# Revit family: BAS-IP_Абонетское устройство_SP-03
name_source: partatom
category: Устройства связи
units: mm (PartAtom-declared; Revit-internal decimal feet)

## family parameters
Всегда вертикально = Да
На основе рабочей плоскости = Нет
Общий = Нет
При загрузке вырезать с полостями = Нет
Размер круглого соединителя = Использовать диаметр
Сохранять ориентацию аннотаций = Нет
Тип детали = Нормальный
Точка расчета площади = Нет

## types (2) — shared parameters
ADSK_Единица измерения = шт.
ADSK_Завод-изготовитель = BAS-IP
ADSK_Количество = 1
ADSK_Наименование = Абонентское IP аудиоустройство
Wi-Fi = 2.4GHz (IEEE 802.11n)
Габаритные размеры = 183 × 105 × 28 мм
Изготовитель = BAS-IP
Количество клавиш управления = 6
Количество поддерживаемых учетных записей VoIP = 1
Метод приемо-передачи аудиосигнала = Full Duplex
Питание = PoE, +12 В
Подключение к сети = 1 PoE порт IEEE 802.3af
Способ настройки и программирования = WEB-интерфейс
Тип поддерживаемого протокола = IPv4
Тип поддерживаемых кодеков = G.711μ / G.711a
Тип установки = Настенный

## per-type parameters (varying)
| type | ADSK_Марка | ADSK_Материал |
| Белый | SP-03 White | White |
| Черный | SP-03 Black | Black |

note: column(s) folded — value = type name in every type: Цветовое решение
